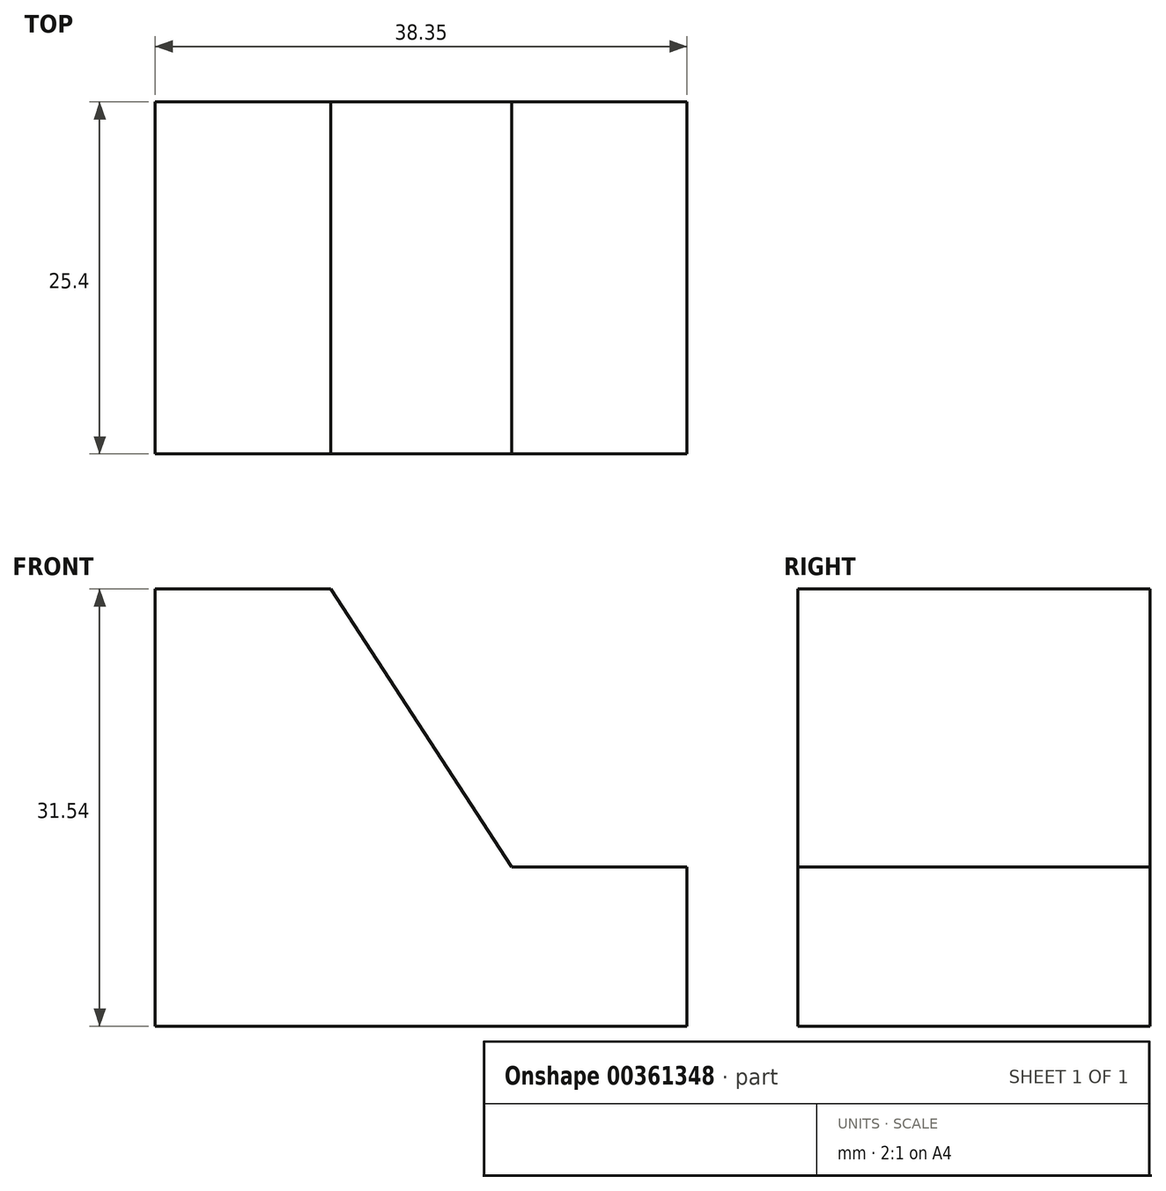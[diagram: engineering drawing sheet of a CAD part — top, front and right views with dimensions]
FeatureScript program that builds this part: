
annotation { "Feature Type Name" : "Feature", "Feature Type Description" : "" }
export const myFeature = defineFeature(function(context is Context, id is Id, definition is map)
    precondition{}
    {
        {
            var Q0;
            Q0=qCreatedBy(makeId("Front.planeOp"),FACE);
            var sketch = newSketch(context, id + "F0", { "sketchPlane" : qUnion([Q0])});
            skLineSegment(sketch, "E0", {"start": v(-33.1, 0) * mm, "end": v(-33.1, 31.54) * mm});
            skLineSegment(sketch, "E1", {"start": v(-33.1, 31.54) * mm, "end": v(-20.44, 31.54) * mm});
            skLineSegment(sketch, "E2", {"start": v(-33.1, 0) * mm, "end": v(5.26, 0) * mm});
            skLineSegment(sketch, "E3", {"start": v(5.26, 0) * mm, "end": v(5.26, 11.49) * mm});
            skLineSegment(sketch, "E4", {"start": v(5.26, 11.49) * mm, "end": v(-7.4, 11.49) * mm});
            skLineSegment(sketch, "E5", {"start": v(-20.44, 31.54) * mm, "end": v(-7.4, 11.49) * mm});
            skSolve(sketch);
        }
        {
            var Q0;
            Q0 = qSketchRegion(id + "F0", true);
            extrude(context, id + "F1", {"entities" : qUnion([Q0]), "depth" : 25.4 * mm});
        }
    });
